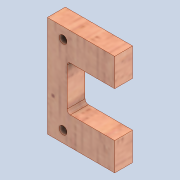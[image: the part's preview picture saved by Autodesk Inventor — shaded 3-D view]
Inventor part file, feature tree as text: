
AUTODESK INVENTOR PART (.ipt)
format: ipt  version: 2020 (Build 240168000, 168)  size: 179,200 bytes
history: native  units: mm
features: other x4, extrude x3, sketch x3, fillet x1, reference x1
ambient origin geometry x8: Origin, YZ Plane, XZ Plane, XY Plane, X Axis, Y Axis, Z Axis, Center Point
bodies: Solid1 (feature_tree)
feature tree (12):
  extrude  "Extrusion1"  Depth=45.0mm
  extrude  "Extrusion3"  TaperAngle=0.0deg  [1 undecoded]
  extrude  "Extrusion4"  Depth=10.0mm TaperAngle=0.0deg
  fillet  "Fillet1"  [1 undecoded]
  sketch  "Sketch1"  dims[d0=30.0mm d1=45.0mm]
  sketch  "Sketch3"  dims[d2=8.0mm d3=0.0mm d8=0.0mm]
  reference  "Reference1"
  sketch  "Sketch4"  dims[d9=20.0mm d10=10.0mm d11=0.0mm d15=0.0mm d16=0.0mm d17=3.5mm d18=3.5mm d19=5.0mm d20=7.0mm d21=5.0mm d22=35.0mm d23=1.5mm]
  parser-record x1  (decoder bookkeeping rows leaked as tree rows — omitted from the tree; the rows remain in map.json)
  other  "0005-00-00 Ansamblu_General.iam"
  other  "Plunger Assembly_Défaut:1"
  other  "plunger_Défaut_4"
note: 2 required parameter values undecoded (feature->parameter linkage not recoverable at this tier; creation-order binding heuristic only, values carry confidence <= 0.55)
note: 1 file-system path scrubbed to <path> (originals preserved in map.json)
